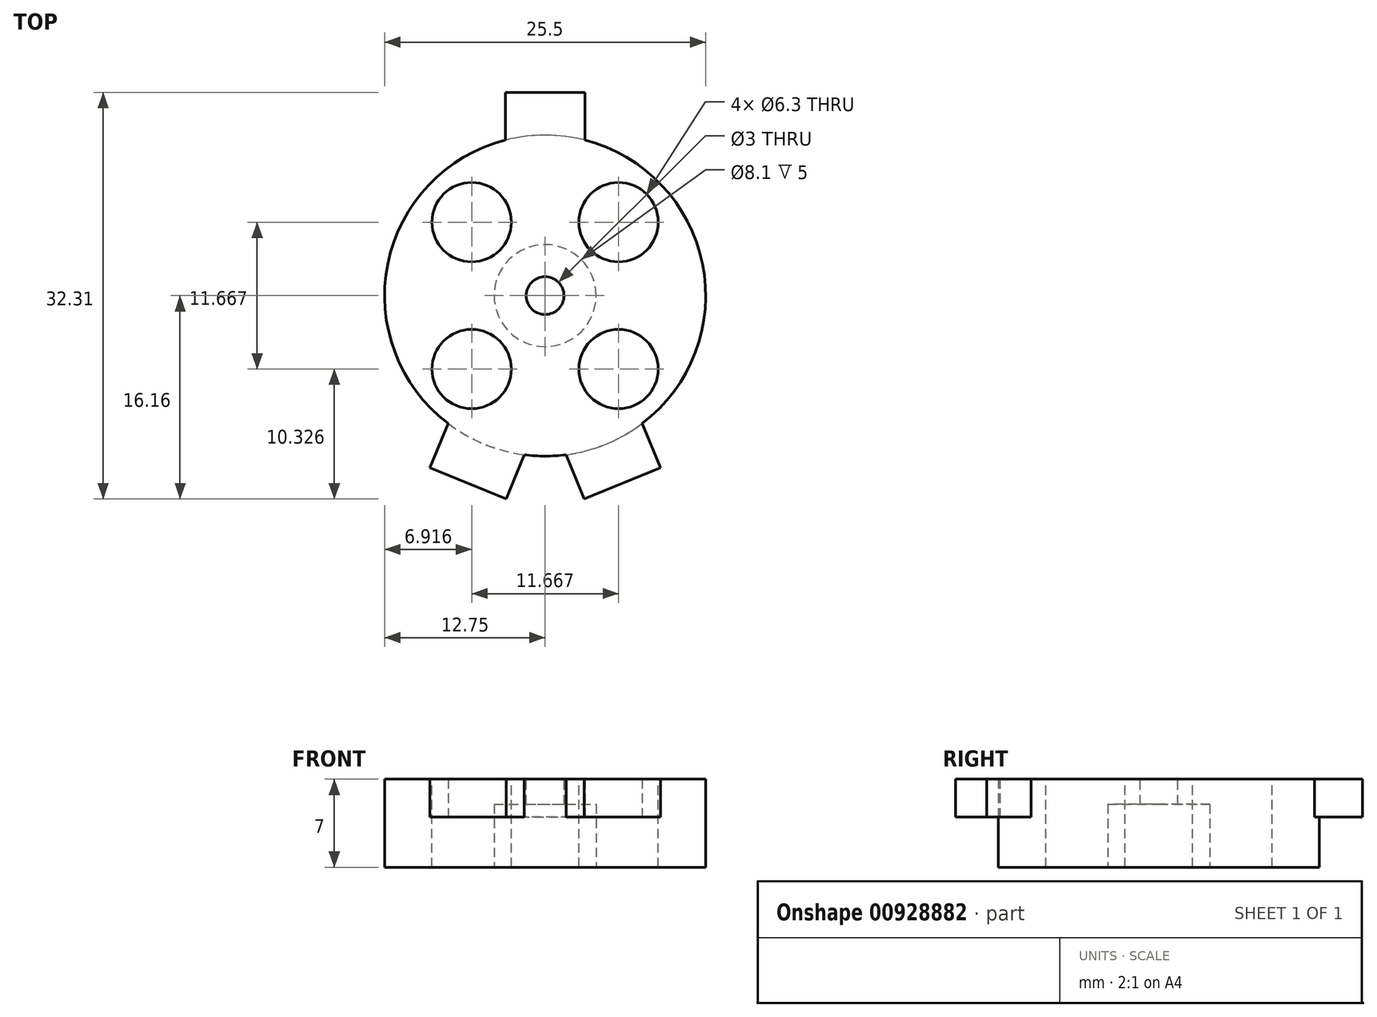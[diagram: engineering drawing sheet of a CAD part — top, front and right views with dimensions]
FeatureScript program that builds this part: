
annotation { "Feature Type Name" : "Feature", "Feature Type Description" : "" }
export const myFeature = defineFeature(function(context is Context, id is Id, definition is map)
    precondition{}
    {
        {
            var Q0;
            Q0=qCreatedBy(makeId("Top.planeOp"),FACE);
            var sketch = newSketch(context, id + "F0", { "sketchPlane" : qUnion([Q0])});
            skArc(sketch, "E0", {"start": v(7.7, -10.16) * mm, "mid": v(12.5, 2.53) * mm, "end": v(3.15, 12.35) * mm});
            skLineSegment(sketch, "E1", {"start": v(0, 12.75) * mm, "end": v(0, -12.75) * mm, "construction": true});
            skLineSegment(sketch, "E2", {"start": v(-3.15, 16.15) * mm, "end": v(0, 16.15) * mm});
            skLineSegment(sketch, "E3", {"start": v(0, 16.15) * mm, "end": v(3.15, 16.15) * mm});
            skLineSegment(sketch, "E4", {"start": v(-3.15, 16.15) * mm, "end": v(-3.15, 12.35) * mm});
            skLineSegment(sketch, "E5", {"start": v(3.15, 16.15) * mm, "end": v(3.15, 12.35) * mm});
            skLineSegment(sketch, "E6", {"start": v(1.66, -12.64) * mm, "end": v(7.7, -10.16) * mm, "construction": true});
            skLineSegment(sketch, "E7", {"start": v(1.66, -12.64) * mm, "end": v(3.1, -16.16) * mm});
            skLineSegment(sketch, "E8", {"start": v(7.7, -10.16) * mm, "end": v(9.15, -13.67) * mm});
            skLineSegment(sketch, "E9", {"start": v(3.1, -16.16) * mm, "end": v(9.15, -13.67) * mm});
            skLineSegment(sketch, "E10.MirrorCS", {"start": v(-1.66, -12.64) * mm, "end": v(-3.1, -16.16) * mm});
            skLineSegment(sketch, "E11.MirrorCS", {"start": v(-3.1, -16.16) * mm, "end": v(-9.15, -13.67) * mm});
            skLineSegment(sketch, "E12.MirrorCS", {"start": v(-7.7, -10.16) * mm, "end": v(-9.15, -13.67) * mm});
            skArc(sketch, "E13.trimOffspring", {"start": v(-1.66, -12.64) * mm, "mid": v(0, -12.75) * mm, "end": v(1.66, -12.64) * mm});
            skArc(sketch, "E14.trimOffspring", {"start": v(-3.15, 12.35) * mm, "mid": v(-12.5, 2.53) * mm, "end": v(-7.7, -10.16) * mm});
            skLineSegment(sketch, "E15", {"start": v(-1.66, -12.64) * mm, "end": v(1.66, -12.64) * mm, "construction": true});
            skLineSegment(sketch, "E16", {"start": v(-3.1, -16.16) * mm, "end": v(3.1, -16.16) * mm, "construction": true});
            skLineSegment(sketch, "E17", {"start": v(-9.15, -13.67) * mm, "end": v(9.15, -13.67) * mm, "construction": true});
            skLineSegment(sketch, "E18", {"start": v(-7.7, -10.16) * mm, "end": v(7.7, -10.16) * mm, "construction": true});
            skSolve(sketch);
        }
        {
            var Q0;
            Q0=qSketchRegion(id+"F0",true);
            extrude(context, id + "F1", {"entities" : qUnion([Q0]), "depth" : 3 * mm, "offsetDistance" : 25 * mm});
        }
        {
            var Q0;
            Q0=makeQuery(id+"F1.opExtrude","CAP_FACE",FACE,{"disambiguationData":[OSD([sQuery(id+"F0.wireOp",EDGE,"E0"),sQuery(id+"F0.wireOp",EDGE,"E2"),sQuery(id+"F0.wireOp",EDGE,"E3"),sQuery(id+"F0.wireOp",EDGE,"E4"),sQuery(id+"F0.wireOp",EDGE,"E5"),sQuery(id+"F0.wireOp",EDGE,"E7"),sQuery(id+"F0.wireOp",EDGE,"E8"),sQuery(id+"F0.wireOp",EDGE,"E9"),sQuery(id+"F0.wireOp",EDGE,"E10.MirrorCS"),sQuery(id+"F0.wireOp",EDGE,"E11.MirrorCS"),sQuery(id+"F0.wireOp",EDGE,"E12.MirrorCS"),sQuery(id+"F0.wireOp",EDGE,"E13.trimOffspring"),sQuery(id+"F0.wireOp",EDGE,"E14.trimOffspring")])],"isStart":true});
            var sketch = newSketch(context, id + "F2", { "sketchPlane" : qUnion([Q0])});
            skCircle(sketch, "E19", {"center": v(0, 0) * mm, "radius": 12.75 * mm});
            skSolve(sketch);
        }
        {
            var Q0;
            Q0=qSketchRegion(id+"F2",true);
            extrude(context, id + "F3", {"entities" : qUnion([Q0]), "operationType" : NewBodyOperationType.ADD, "depth" : 4 * mm, "offsetDistance" : 25 * mm});
        }
        {
            var Q0;
            Q0=makeQuery(id+"F1.opExtrude","CAP_FACE",FACE,{"disambiguationData":[OSD([sQuery(id+"F0.wireOp",EDGE,"E0"),sQuery(id+"F0.wireOp",EDGE,"E2"),sQuery(id+"F0.wireOp",EDGE,"E3"),sQuery(id+"F0.wireOp",EDGE,"E4"),sQuery(id+"F0.wireOp",EDGE,"E5"),sQuery(id+"F0.wireOp",EDGE,"E7"),sQuery(id+"F0.wireOp",EDGE,"E8"),sQuery(id+"F0.wireOp",EDGE,"E9"),sQuery(id+"F0.wireOp",EDGE,"E10.MirrorCS"),sQuery(id+"F0.wireOp",EDGE,"E11.MirrorCS"),sQuery(id+"F0.wireOp",EDGE,"E12.MirrorCS"),sQuery(id+"F0.wireOp",EDGE,"E13.trimOffspring"),sQuery(id+"F0.wireOp",EDGE,"E14.trimOffspring")])],"isStart":false});
            var sketch = newSketch(context, id + "F4", { "sketchPlane" : qUnion([Q0])});
            skLineSegment(sketch, "E20", {"start": v(-12.75, 0) * mm, "end": v(0, 0) * mm, "construction": true});
            skLineSegment(sketch, "E21", {"start": v(0, 0) * mm, "end": v(-2.65, 2.65) * mm, "construction": true});
            skLineSegment(sketch, "E22", {"start": v(0, 0) * mm, "end": v(9.02, -9.02) * mm, "construction": true});
            skLineSegment(sketch, "E23.MirrorCS", {"start": v(0, 0) * mm, "end": v(9.02, 9.02) * mm, "construction": true});
            skLineSegment(sketch, "E24.MirrorCS", {"start": v(0, 0) * mm, "end": v(-9.02, -9.02) * mm, "construction": true});
            skCircle(sketch, "E25", {"center": v(-5.83, 5.83) * mm, "radius": 3.15 * mm});
            skCircle(sketch, "E26.1.0", {"center": v(-5.83, -5.83) * mm, "radius": 3.15 * mm});
            skCircle(sketch, "E26.2.0", {"center": v(5.83, -5.83) * mm, "radius": 3.15 * mm});
            skCircle(sketch, "E26.3.0", {"center": v(5.83, 5.83) * mm, "radius": 3.15 * mm});
            skLineSegment(sketch, "E27", {"start": v(-2.65, 2.65) * mm, "end": v(-9.02, 9.02) * mm, "construction": true});
            skCircle(sketch, "E28", {"center": v(0, 0) * mm, "radius": 1.5 * mm});
            skSolve(sketch);
        }
        {
            var Q0;
            Q0=qSketchRegion(id+"F4",true);
            var Q1;
            Q1=makeQuery(id+"F1.opExtrude","CAP_FACE",FACE,{"disambiguationData":[OSD([sQuery(id+"F0.wireOp",EDGE,"E0"),sQuery(id+"F0.wireOp",EDGE,"E2"),sQuery(id+"F0.wireOp",EDGE,"E3"),sQuery(id+"F0.wireOp",EDGE,"E4"),sQuery(id+"F0.wireOp",EDGE,"E5"),sQuery(id+"F0.wireOp",EDGE,"E7"),sQuery(id+"F0.wireOp",EDGE,"E8"),sQuery(id+"F0.wireOp",EDGE,"E9"),sQuery(id+"F0.wireOp",EDGE,"E10.MirrorCS"),sQuery(id+"F0.wireOp",EDGE,"E11.MirrorCS"),sQuery(id+"F0.wireOp",EDGE,"E12.MirrorCS"),sQuery(id+"F0.wireOp",EDGE,"E13.trimOffspring"),sQuery(id+"F0.wireOp",EDGE,"E14.trimOffspring")])],"isStart":true});
            extrude(context, id + "F5", {"entities" : qUnion([Q0]), "operationType" : NewBodyOperationType.REMOVE, "oppositeDirection" : true, "depth" : 25 * mm, "endBoundEntityFace" : qUnion([Q1]), "offsetDistance" : 25 * mm});
        }
        {
            var Q0;
            Q0=makeQuery(id+"F3.opExtrude","CAP_FACE",FACE,{"disambiguationData":[OSD([sQuery(id+"F2.wireOp",EDGE,"E19")])],"isStart":false});
            var sketch = newSketch(context, id + "F6", { "sketchPlane" : qUnion([Q0])});
            skCircle(sketch, "E29", {"center": v(0, 0) * mm, "radius": 4.05 * mm});
            skSolve(sketch);
        }
        {
            var Q0;
            Q0=qSketchRegion(id+"F6",true);
            extrude(context, id + "F7", {"entities" : qUnion([Q0]), "operationType" : NewBodyOperationType.REMOVE, "oppositeDirection" : true, "depth" : 5 * mm, "offsetDistance" : 25 * mm});
        }
    });
